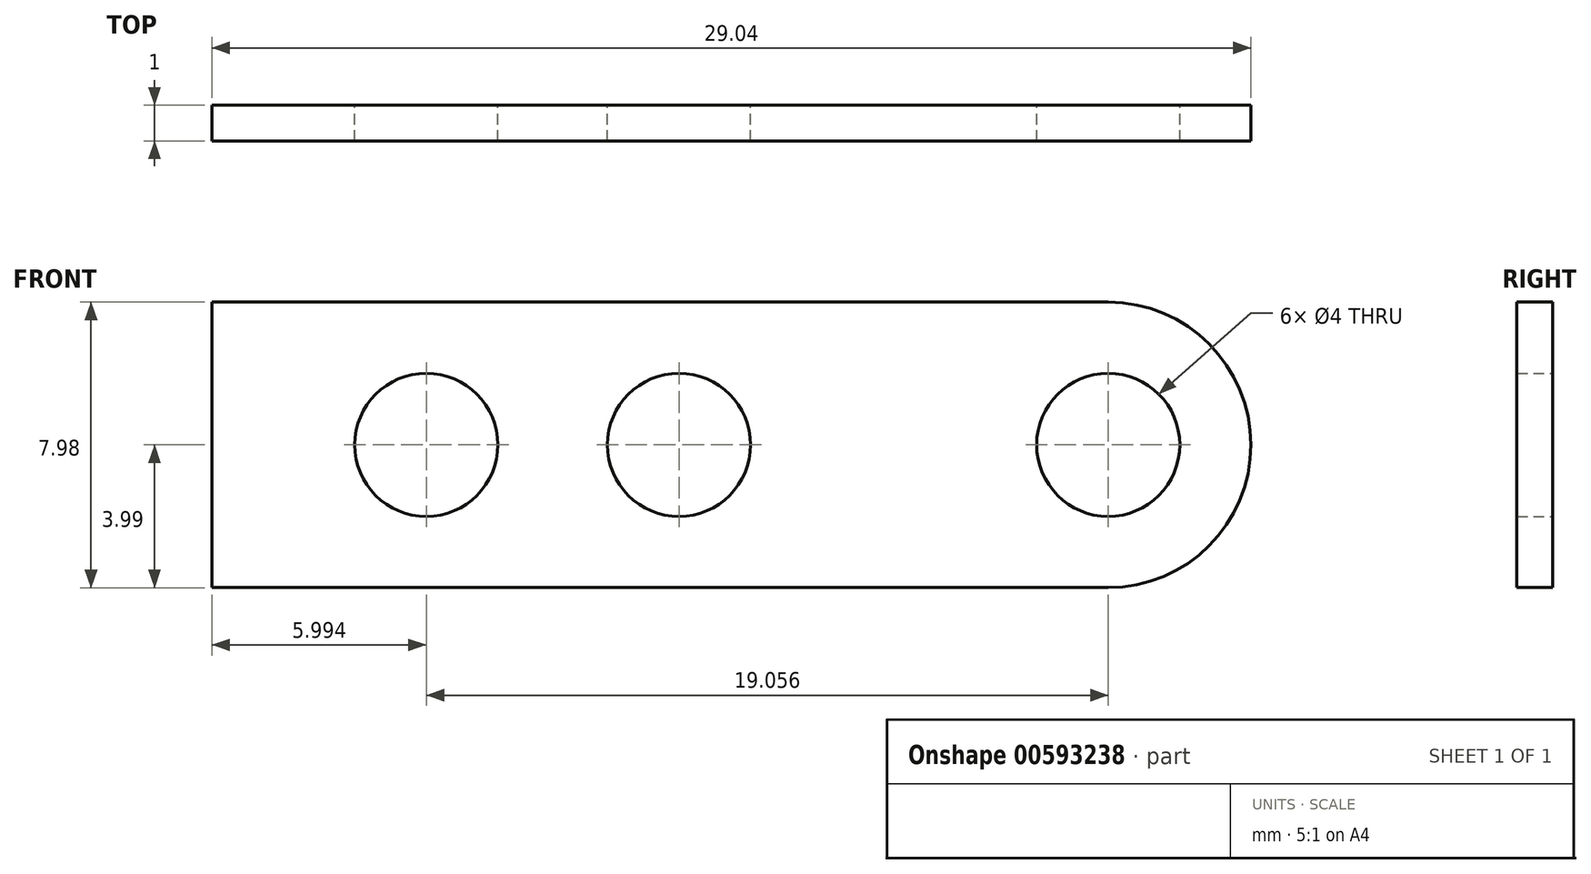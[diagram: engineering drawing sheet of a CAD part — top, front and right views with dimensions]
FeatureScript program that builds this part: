
annotation { "Feature Type Name" : "Feature", "Feature Type Description" : "" }
export const myFeature = defineFeature(function(context is Context, id is Id, definition is map)
    precondition{}
    {
        {
            var Q0;
            Q0=qCreatedBy(makeId("Front.planeOp"),FACE);
            var sketch = newSketch(context, id + "F0", { "sketchPlane" : qUnion([Q0])});
            skCircle(sketch, "E0", {"center": v(0, 0) * mm, "radius": 2 * mm});
            skArc(sketch, "E1", {"start": v(0, -3.99) * mm, "mid": v(3.99, 0) * mm, "end": v(0, 3.99) * mm});
            skLineSegment(sketch, "E2", {"start": v(0, 3.99) * mm, "end": v(-25.05, 3.99) * mm});
            skLineSegment(sketch, "E3", {"start": v(-25.05, 3.99) * mm, "end": v(-25.05, -3.99) * mm});
            skLineSegment(sketch, "E4", {"start": v(-25.05, -3.99) * mm, "end": v(0, -3.99) * mm});
            skCircle(sketch, "E5", {"center": v(-19.06, 0) * mm, "radius": 2 * mm});
            skCircle(sketch, "E6", {"center": v(-12, 0) * mm, "radius": 2 * mm});
            skLineSegment(sketch, "E7", {"start": v(-6, 3.99) * mm, "end": v(-6, -3.99) * mm, "construction": true});
            skLineSegment(sketch, "E8", {"start": v(-4, 3.99) * mm, "end": v(-4, -3.99) * mm, "construction": true});
            skSolve(sketch);
        }
        {
            var Q0;
            Q0=qSketchRegion(id+"F0",true);
            extrude(context, id + "F1", {"entities" : qUnion([Q0]), "endBound" : BoundingType.SYMMETRIC, "depth" : 1 * mm});
        }
    });
